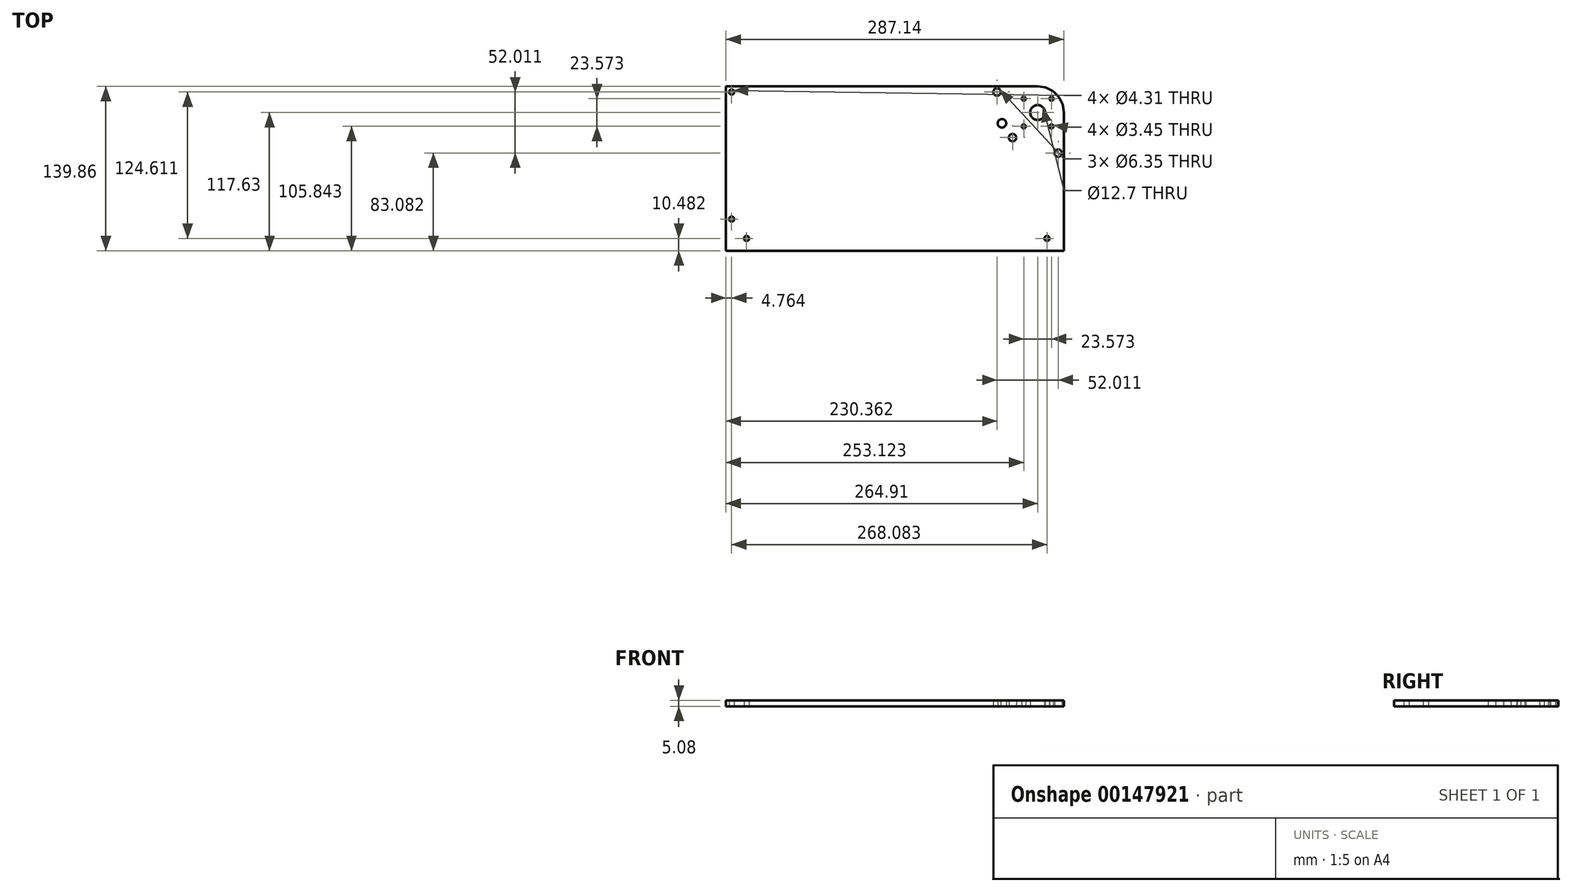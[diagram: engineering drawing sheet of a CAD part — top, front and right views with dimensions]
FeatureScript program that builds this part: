
annotation { "Feature Type Name" : "Feature", "Feature Type Description" : "" }
export const myFeature = defineFeature(function(context is Context, id is Id, definition is map)
    precondition{}
    {
        {
            var Q0;
            Q0=qCreatedBy(makeId("Top.planeOp"),FACE);
            var sketch = newSketch(context, id + "F0", { "sketchPlane" : qUnion([Q0])});
            skCircle(sketch, "E0", {"center": v(0, 0) * mm, "radius": 6.35 * mm});
            skLineSegment(sketch, "E1.bottom", {"start": v(-264.9, 22.22) * mm, "end": v(0, 22.23) * mm});
            skLineSegment(sketch, "E1.top", {"start": v(-264.9, -117.63) * mm, "end": v(22.23, -117.63) * mm});
            skLineSegment(sketch, "E1.left", {"start": v(-264.9, 22.22) * mm, "end": v(-264.9, -117.63) * mm});
            skArc(sketch, "E2", {"start": v(22.23, 0) * mm, "mid": v(15.72, 15.72) * mm, "end": v(0, 22.23) * mm});
            skLineSegment(sketch, "E3", {"start": v(22.23, -117.63) * mm, "end": v(22.23, -96.67) * mm});
            skLineSegment(sketch, "E4", {"start": v(22.23, -96.67) * mm, "end": v(22.23, 0) * mm});
            skLineSegment(sketch, "E5", {"start": v(22.23, -107.15) * mm, "end": v(7.94, -107.15) * mm, "construction": true});
            skCircle(sketch, "E6", {"center": v(7.94, -107.15) * mm, "radius": 2.15 * mm});
            skLineSegment(sketch, "E7", {"start": v(-264.9, -107.15) * mm, "end": v(-247.45, -107.15) * mm, "construction": true});
            skCircle(sketch, "E8", {"center": v(-247.45, -107.15) * mm, "radius": 2.15 * mm});
            skCircle(sketch, "E9", {"center": v(-260.15, 17.46) * mm, "radius": 2.15 * mm});
            skLineSegment(sketch, "E10", {"start": v(-260.15, 17.46) * mm, "end": v(-260.15, -90.64) * mm, "construction": true});
            skLineSegment(sketch, "E11", {"start": v(-260.15, -90.64) * mm, "end": v(-260.15, -107.15) * mm, "construction": true});
            skCircle(sketch, "E12", {"center": v(-260.15, -90.64) * mm, "radius": 2.15 * mm});
            skLineSegment(sketch, "E13", {"start": v(0, 0) * mm, "end": v(17.46, -34.55) * mm, "construction": true});
            skLineSegment(sketch, "E14", {"start": v(0, 0) * mm, "end": v(-34.55, 17.46) * mm, "construction": true});
            skLineSegment(sketch, "E15", {"start": v(0, 0) * mm, "end": v(-21.33, -21.33) * mm, "construction": true});
            skLineSegment(sketch, "E16", {"start": v(-21.33, -21.33) * mm, "end": v(17.46, -34.55) * mm, "construction": true});
            skLineSegment(sketch, "E17", {"start": v(-21.33, -21.33) * mm, "end": v(-34.55, 17.46) * mm, "construction": true});
            skCircle(sketch, "E18", {"center": v(-34.55, 17.46) * mm, "radius": 4.76 * mm, "construction": true});
            skCircle(sketch, "E19", {"center": v(-34.55, 17.46) * mm, "radius": 3.18 * mm});
            skCircle(sketch, "E20", {"center": v(-21.33, -21.33) * mm, "radius": 3.18 * mm});
            skCircle(sketch, "E21", {"center": v(17.46, -34.55) * mm, "radius": 3.18 * mm});
            skLineSegment(sketch, "E22", {"start": v(-260.15, 17.46) * mm, "end": v(-260.15, 22.22) * mm, "construction": true});
            skLineSegment(sketch, "E23", {"start": v(-260.15, 17.46) * mm, "end": v(-264.9, 17.46) * mm, "construction": true});
            skCircle(sketch, "E24", {"center": v(17.46, -34.55) * mm, "radius": 4.76 * mm, "construction": true});
            skLineSegment(sketch, "E25", {"start": v(-1.93, -27.94) * mm, "end": v(-3.47, -32.45) * mm, "construction": true});
            skLineSegment(sketch, "E26", {"start": v(15.93, -39.06) * mm, "end": v(-3.47, -32.45) * mm, "construction": true});
            skLineSegment(sketch, "E27", {"start": v(0, 0) * mm, "end": v(-30.36, -9.16) * mm, "construction": true});
            skCircle(sketch, "E28", {"center": v(-30.36, -9.16) * mm, "radius": 3.66 * mm});
            skLineSegment(sketch, "E29.bottom", {"start": v(11.79, 11.79) * mm, "end": v(-11.79, 11.79) * mm, "construction": true});
            skLineSegment(sketch, "E29.top", {"start": v(11.79, -11.79) * mm, "end": v(-11.79, -11.79) * mm, "construction": true});
            skLineSegment(sketch, "E29.left", {"start": v(11.79, 11.79) * mm, "end": v(11.79, -11.79) * mm, "construction": true});
            skLineSegment(sketch, "E29.right", {"start": v(-11.79, 11.79) * mm, "end": v(-11.79, -11.79) * mm, "construction": true});
            skCircle(sketch, "E30", {"center": v(-11.79, 11.79) * mm, "radius": 1.73 * mm});
            skCircle(sketch, "E31", {"center": v(11.79, 11.79) * mm, "radius": 1.73 * mm});
            skCircle(sketch, "E32", {"center": v(11.79, -11.79) * mm, "radius": 1.73 * mm});
            skCircle(sketch, "E33", {"center": v(-11.79, -11.79) * mm, "radius": 1.73 * mm});
            skSolve(sketch);
        }
        {
            var Q0;
            Q0=qSketchRegion(id+"F0",true);
            extrude(context, id + "F1", {"entities" : qUnion([Q0]), "depth" : 5.08 * mm});
        }
    });
